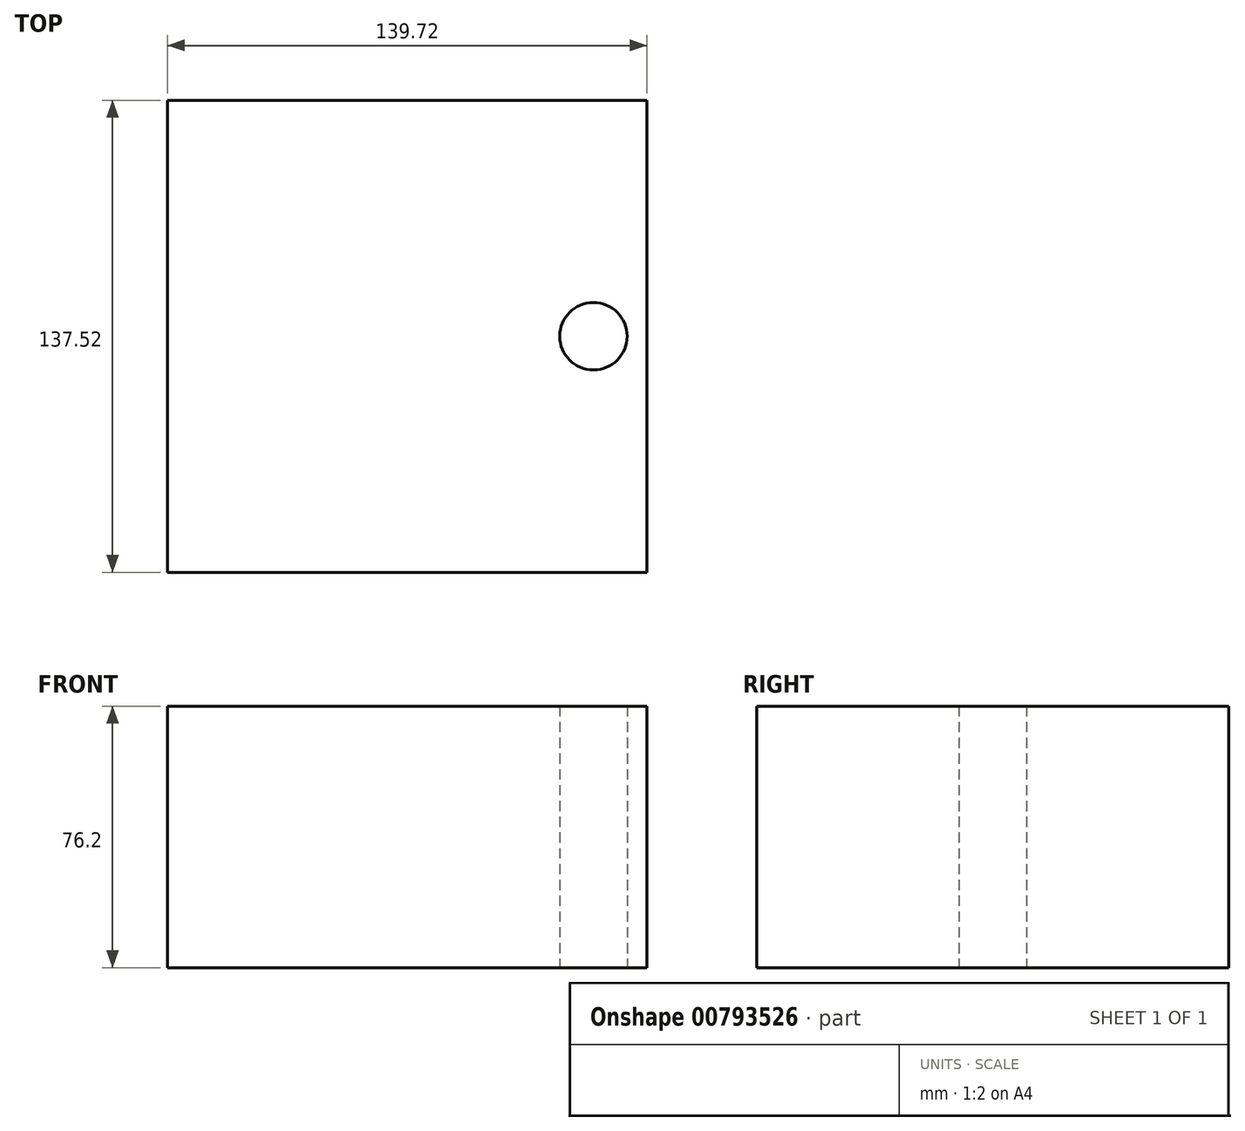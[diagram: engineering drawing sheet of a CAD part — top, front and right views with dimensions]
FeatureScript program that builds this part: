
annotation { "Feature Type Name" : "Feature", "Feature Type Description" : "" }
export const myFeature = defineFeature(function(context is Context, id is Id, definition is map)
    precondition{}
    {
        {
            var Q0;
            Q0=qCreatedBy(makeId("Top.planeOp"),FACE);
            var sketch = newSketch(context, id + "F0", { "sketchPlane" : qUnion([Q0])});
            skLineSegment(sketch, "E0.bottom", {"start": v(69.86, -68.76) * mm, "end": v(-69.86, -68.76) * mm});
            skLineSegment(sketch, "E0.top", {"start": v(69.86, 68.76) * mm, "end": v(-69.86, 68.76) * mm});
            skLineSegment(sketch, "E0.left", {"start": v(69.86, -68.76) * mm, "end": v(69.86, 68.76) * mm});
            skLineSegment(sketch, "E0.right", {"start": v(-69.86, -68.76) * mm, "end": v(-69.86, 68.76) * mm});
            skPoint(sketch, "E0.middle", {"position": v(0, 0) * mm});
            skLineSegment(sketch, "E1", {"start": v(0, 68.76) * mm, "end": v(0, -68.76) * mm});
            skSolve(sketch);
        }
        {
            var Q0;
            Q0=qCreatedBy(makeId("Top.planeOp"),FACE);
            var sketch = newSketch(context, id + "F1", { "sketchPlane" : qUnion([Q0])});
            skCircle(sketch, "E2", {"center": v(54.26, 0) * mm, "radius": 9.82 * mm});
            skSolve(sketch);
        }
        {
            var Q0;
            Q0=makeQuery(id+"F1.imprint","IMPRINT",FACE,{"disambiguationData":[TD([[makeQuery(id+"F1.imprint","IMPRINT",EDGE,{"derivedFrom":sQuery(id+"F1.wireOp",EDGE,"E2")}),1.0]])]});
            var Q1;
            {var subQ0=sQuery(id+"F0.wireOp",EDGE,"E0.left");Q1=makeQuery(id+"F0.imprint","IMPRINT",FACE,{"disambiguationData":[TD([[makeQuery(id+"F0.imprint","IMPRINT",EDGE,{"derivedFrom":subQ0}),1.0]])]});}
            var Q2;
            {var subQ0=sQuery(id+"F0.wireOp",EDGE,"E0.right");Q2=makeQuery(id+"F0.imprint","IMPRINT",FACE,{"disambiguationData":[TD([[makeQuery(id+"F0.imprint","IMPRINT",EDGE,{"derivedFrom":subQ0}),-1.0]])]});}
            extrude(context, id + "F2", {"entities" : qUnion([Q0, Q1, Q2]), "depth" : 76.2 * mm, "offsetDistance" : 25.4 * mm});
        }
    });
